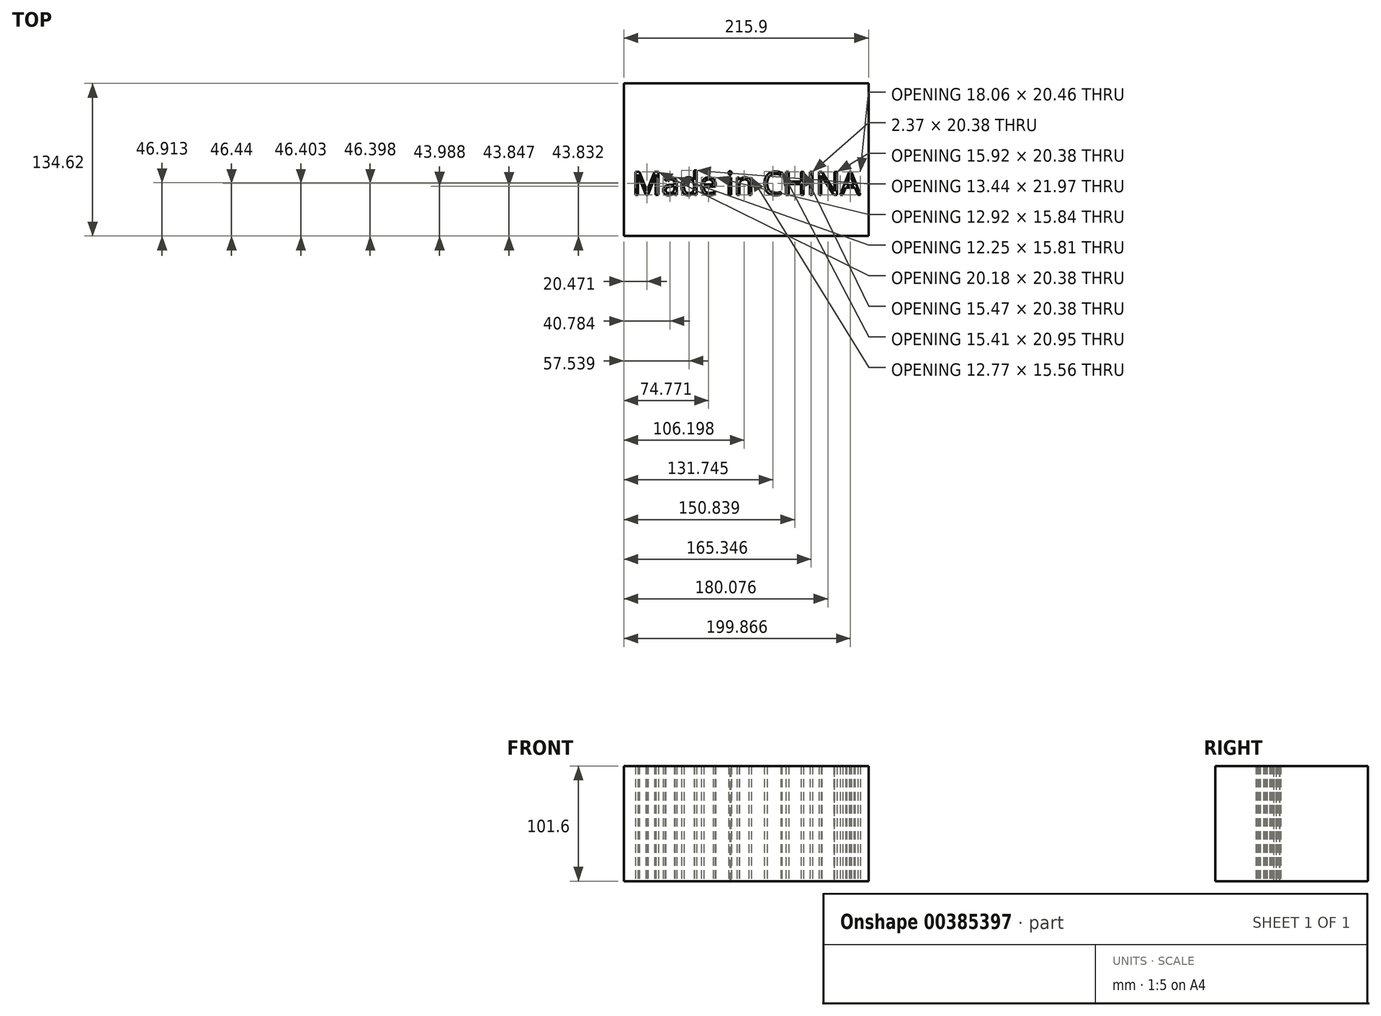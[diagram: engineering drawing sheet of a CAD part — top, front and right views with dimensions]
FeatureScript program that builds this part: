
annotation { "Feature Type Name" : "Feature", "Feature Type Description" : "" }
export const myFeature = defineFeature(function(context is Context, id is Id, definition is map)
    precondition{}
    {
        {
            var Q0;
            Q0=qCreatedBy(makeId("Top.planeOp"),FACE);
            var sketch = newSketch(context, id + "F0", { "sketchPlane" : qUnion([Q0])});
            skLineSegment(sketch, "E0.bottom", {"start": v(-102.22, 48.45) * mm, "end": v(113.68, 48.45) * mm});
            skLineSegment(sketch, "E0.top", {"start": v(-102.22, -86.17) * mm, "end": v(113.68, -86.17) * mm});
            skLineSegment(sketch, "E0.left", {"start": v(-102.22, 48.45) * mm, "end": v(-102.22, -86.17) * mm});
            skLineSegment(sketch, "E0.right", {"start": v(113.68, 48.45) * mm, "end": v(113.68, -86.17) * mm});
            skLineSegment(sketch, "E1.bottom", {"start": v(62.88, 48.45) * mm, "end": v(-51.42, 48.45) * mm});
            skLineSegment(sketch, "E1.top", {"start": v(62.88, 226.25) * mm, "end": v(-51.42, 226.25) * mm});
            skLineSegment(sketch, "E1.left", {"start": v(62.88, 48.45) * mm, "end": v(62.88, 226.25) * mm});
            skLineSegment(sketch, "E1.right", {"start": v(-51.42, 48.45) * mm, "end": v(-51.42, 226.25) * mm});
            skText(sketch, "E2", { "text": "Made in CHINA", "fontName": "OpenSans-Regular.ttf"});
            const initialGuessF0  = {"E2": [-0.09464, -0.04996, 1, 0, 0.02055]};
            skSetInitialGuess(sketch, initialGuessF0);
            skSolve(sketch);
        }
        {
            var Q0;
            Q0=makeQuery(id+"F0.imprint","IMPRINT",FACE,{"disambiguationData":[TD([[makeQuery(id+"F0.imprint","IMPRINT",EDGE,{"derivedFrom":sQuery(id+"F0.wireOp",EDGE,"E1.bottom")}),-1.0]])]});
            var Q1;
            Q1=makeQuery(id+"F0.imprint","IMPRINT",FACE,{"disambiguationData":[TD([[makeQuery(id+"F0.imprint","IMPRINT",EDGE,{"derivedFrom":sQuery(id+"F0.wireOp",EDGE,"E2.sketch_text.stroke-45")}),-1.0]])]});
            var Q2;
            Q2=makeQuery(id+"F0.imprint","IMPRINT",FACE,{"disambiguationData":[TD([[makeQuery(id+"F0.imprint","IMPRINT",EDGE,{"derivedFrom":sQuery(id+"F0.wireOp",EDGE,"E2.sketch_text.stroke-60")}),1.0]])]});
            var Q3;
            Q3=makeQuery(id+"F0.imprint","IMPRINT",FACE,{"disambiguationData":[TD([[makeQuery(id+"F0.imprint","IMPRINT",EDGE,{"derivedFrom":sQuery(id+"F0.wireOp",EDGE,"E2.sketch_text.stroke-69")}),-1.0]])]});
            var Q4;
            Q4=makeQuery(id+"F0.imprint","IMPRINT",FACE,{"disambiguationData":[TD([[makeQuery(id+"F0.imprint","IMPRINT",EDGE,{"derivedFrom":sQuery(id+"F0.wireOp",EDGE,"E2.sketch_text.stroke-18")}),-1.0]])]});
            var Q5;
            Q5=makeQuery(id+"F0.imprint","IMPRINT",FACE,{"disambiguationData":[TD([[makeQuery(id+"F0.imprint","IMPRINT",EDGE,{"derivedFrom":sQuery(id+"F0.wireOp",EDGE,"E2.sketch_text.stroke-0")}),-1.0]])]});
            var Q6;
            Q6=makeQuery(id+"F0.imprint","IMPRINT",FACE,{"disambiguationData":[TD([[makeQuery(id+"F0.imprint","IMPRINT",EDGE,{"derivedFrom":sQuery(id+"F0.wireOp",EDGE,"E2.sketch_text.stroke-37")}),1.0]])]});
            var Q7;
            Q7=makeQuery(id+"F0.imprint","IMPRINT",FACE,{"disambiguationData":[TD([[makeQuery(id+"F0.imprint","IMPRINT",EDGE,{"derivedFrom":sQuery(id+"F0.wireOp",EDGE,"E2.sketch_text.stroke-83")}),1.0]])]});
            var Q8;
            Q8=makeQuery(id+"F0.imprint","IMPRINT",FACE,{"disambiguationData":[TD([[makeQuery(id+"F0.imprint","IMPRINT",EDGE,{"derivedFrom":sQuery(id+"F0.wireOp",EDGE,"E2.sketch_text.stroke-100")}),-1.0]])]});
            var Q9;
            Q9=makeQuery(id+"F0.imprint","IMPRINT",FACE,{"disambiguationData":[TD([[makeQuery(id+"F0.imprint","IMPRINT",EDGE,{"derivedFrom":sQuery(id+"F0.wireOp",EDGE,"E2.sketch_text.stroke-88")}),-1.0]])]});
            var Q10;
            Q10=makeQuery(id+"F0.imprint","IMPRINT",FACE,{"disambiguationData":[TD([[makeQuery(id+"F0.imprint","IMPRINT",EDGE,{"derivedFrom":sQuery(id+"F0.wireOp",EDGE,"E0.top")}),1.0]])]});
            var Q11;
            Q11=makeQuery(id+"F0.imprint","IMPRINT",FACE,{"disambiguationData":[TD([[makeQuery(id+"F0.imprint","IMPRINT",EDGE,{"derivedFrom":sQuery(id+"F0.wireOp",EDGE,"E2.sketch_text.stroke-92")}),-1.0]])]});
            var Q12;
            Q12=makeQuery(id+"F0.imprint","IMPRINT",FACE,{"disambiguationData":[TD([[makeQuery(id+"F0.imprint","IMPRINT",EDGE,{"derivedFrom":sQuery(id+"F0.wireOp",EDGE,"E2.sketch_text.stroke-117")}),-1.0]])]});
            var Q13;
            Q13=makeQuery(id+"F0.imprint","IMPRINT",FACE,{"disambiguationData":[TD([[makeQuery(id+"F0.imprint","IMPRINT",EDGE,{"derivedFrom":sQuery(id+"F0.wireOp",EDGE,"E2.sketch_text.stroke-132")}),-1.0]])]});
            var Q14;
            Q14=makeQuery(id+"F0.imprint","IMPRINT",FACE,{"disambiguationData":[TD([[makeQuery(id+"F0.imprint","IMPRINT",EDGE,{"derivedFrom":sQuery(id+"F0.wireOp",EDGE,"E2.sketch_text.stroke-148")}),-1.0]])]});
            var Q15;
            Q15=makeQuery(id+"F0.imprint","IMPRINT",FACE,{"disambiguationData":[TD([[makeQuery(id+"F0.imprint","IMPRINT",EDGE,{"derivedFrom":sQuery(id+"F0.wireOp",EDGE,"E2.sketch_text.stroke-144")}),-1.0]])]});
            var Q16;
            Q16=makeQuery(id+"F0.imprint","IMPRINT",FACE,{"disambiguationData":[TD([[makeQuery(id+"F0.imprint","IMPRINT",EDGE,{"derivedFrom":sQuery(id+"F0.wireOp",EDGE,"E2.sketch_text.stroke-171")}),1.0]])]});
            var Q17;
            Q17=makeQuery(id+"F0.imprint","IMPRINT",FACE,{"disambiguationData":[TD([[makeQuery(id+"F0.imprint","IMPRINT",EDGE,{"derivedFrom":sQuery(id+"F0.wireOp",EDGE,"E2.sketch_text.stroke-163")}),-1.0]])]});
            extrude(context, id + "F1", {"entities" : qUnion([Q0, Q1, Q2, Q3, Q4, Q5, Q6, Q7, Q8, Q9, Q10, Q11, Q12, Q13, Q14, Q15, Q16, Q17]), "depth" : 101.6 * mm});
        }
        {
            var Q0;
            Q0=makeQuery(id+"F0.imprint","IMPRINT",FACE,{"disambiguationData":[TD([[makeQuery(id+"F0.imprint","IMPRINT",EDGE,{"derivedFrom":sQuery(id+"F0.wireOp",EDGE,"E2.sketch_text.stroke-100")}),-1.0]])]});
            var Q1;
            Q1=makeQuery(id+"F0.imprint","IMPRINT",FACE,{"disambiguationData":[TD([[makeQuery(id+"F0.imprint","IMPRINT",EDGE,{"derivedFrom":sQuery(id+"F0.wireOp",EDGE,"E2.sketch_text.stroke-45")}),-1.0]])]});
            var Q2;
            Q2=makeQuery(id+"F0.imprint","IMPRINT",FACE,{"disambiguationData":[TD([[makeQuery(id+"F0.imprint","IMPRINT",EDGE,{"derivedFrom":sQuery(id+"F0.wireOp",EDGE,"E2.sketch_text.stroke-69")}),-1.0]])]});
            var Q3;
            Q3=makeQuery(id+"F0.imprint","IMPRINT",FACE,{"disambiguationData":[TD([[makeQuery(id+"F0.imprint","IMPRINT",EDGE,{"derivedFrom":sQuery(id+"F0.wireOp",EDGE,"E2.sketch_text.stroke-88")}),-1.0]])]});
            var Q4;
            Q4=makeQuery(id+"F0.imprint","IMPRINT",FACE,{"disambiguationData":[TD([[makeQuery(id+"F0.imprint","IMPRINT",EDGE,{"derivedFrom":sQuery(id+"F0.wireOp",EDGE,"E2.sketch_text.stroke-92")}),-1.0]])]});
            var Q5;
            Q5=makeQuery(id+"F0.imprint","IMPRINT",FACE,{"disambiguationData":[TD([[makeQuery(id+"F0.imprint","IMPRINT",EDGE,{"derivedFrom":sQuery(id+"F0.wireOp",EDGE,"E2.sketch_text.stroke-18")}),-1.0]])]});
            var Q6;
            Q6=makeQuery(id+"F0.imprint","IMPRINT",FACE,{"disambiguationData":[TD([[makeQuery(id+"F0.imprint","IMPRINT",EDGE,{"derivedFrom":sQuery(id+"F0.wireOp",EDGE,"E2.sketch_text.stroke-0")}),-1.0]])]});
            var Q7;
            Q7=makeQuery(id+"F0.imprint","IMPRINT",FACE,{"disambiguationData":[TD([[makeQuery(id+"F0.imprint","IMPRINT",EDGE,{"derivedFrom":sQuery(id+"F0.wireOp",EDGE,"E2.sketch_text.stroke-132")}),-1.0]])]});
            var Q8;
            Q8=makeQuery(id+"F0.imprint","IMPRINT",FACE,{"disambiguationData":[TD([[makeQuery(id+"F0.imprint","IMPRINT",EDGE,{"derivedFrom":sQuery(id+"F0.wireOp",EDGE,"E2.sketch_text.stroke-117")}),-1.0]])]});
            var Q9;
            Q9=makeQuery(id+"F0.imprint","IMPRINT",FACE,{"disambiguationData":[TD([[makeQuery(id+"F0.imprint","IMPRINT",EDGE,{"derivedFrom":sQuery(id+"F0.wireOp",EDGE,"E2.sketch_text.stroke-163")}),-1.0]])]});
            var Q10;
            Q10=makeQuery(id+"F0.imprint","IMPRINT",FACE,{"disambiguationData":[TD([[makeQuery(id+"F0.imprint","IMPRINT",EDGE,{"derivedFrom":sQuery(id+"F0.wireOp",EDGE,"E2.sketch_text.stroke-144")}),-1.0]])]});
            var Q11;
            Q11=makeQuery(id+"F0.imprint","IMPRINT",FACE,{"disambiguationData":[TD([[makeQuery(id+"F0.imprint","IMPRINT",EDGE,{"derivedFrom":sQuery(id+"F0.wireOp",EDGE,"E2.sketch_text.stroke-148")}),-1.0]])]});
            extrude(context, id + "F2", {"entities" : qUnion([Q0, Q1, Q2, Q3, Q4, Q5, Q6, Q7, Q8, Q9, Q10, Q11]), "operationType" : NewBodyOperationType.REMOVE, "depth" : 254 * mm});
        }
    });
